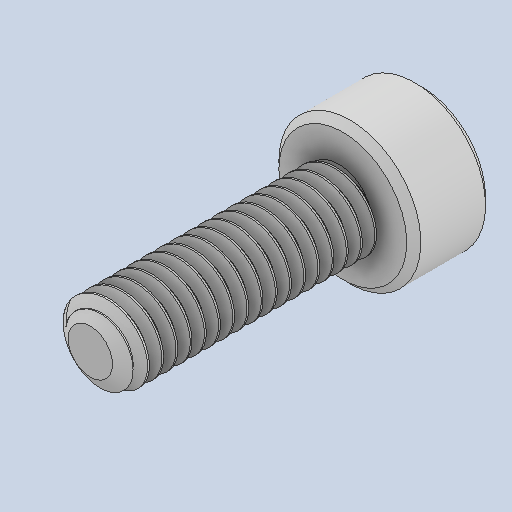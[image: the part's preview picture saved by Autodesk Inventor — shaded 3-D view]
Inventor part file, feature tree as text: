
AUTODESK INVENTOR PART (.ipt)
format: ipt  version: 2023 (Build 270158000, 158)  size: 664,576 bytes
history: native  units: mm
features: chamfer x1
ambient origin geometry x8: Origin, YZ Plane, XZ Plane, XY Plane, X Axis, Y Axis, Z Axis, Center Point
bodies: Solid1 (feature_tree)
feature tree (1):
  chamfer  "Chamfer1"  [1 undecoded]
note: 1 required parameter value undecoded (feature->parameter linkage not recoverable at this tier; creation-order binding heuristic only, values carry confidence <= 0.55)
